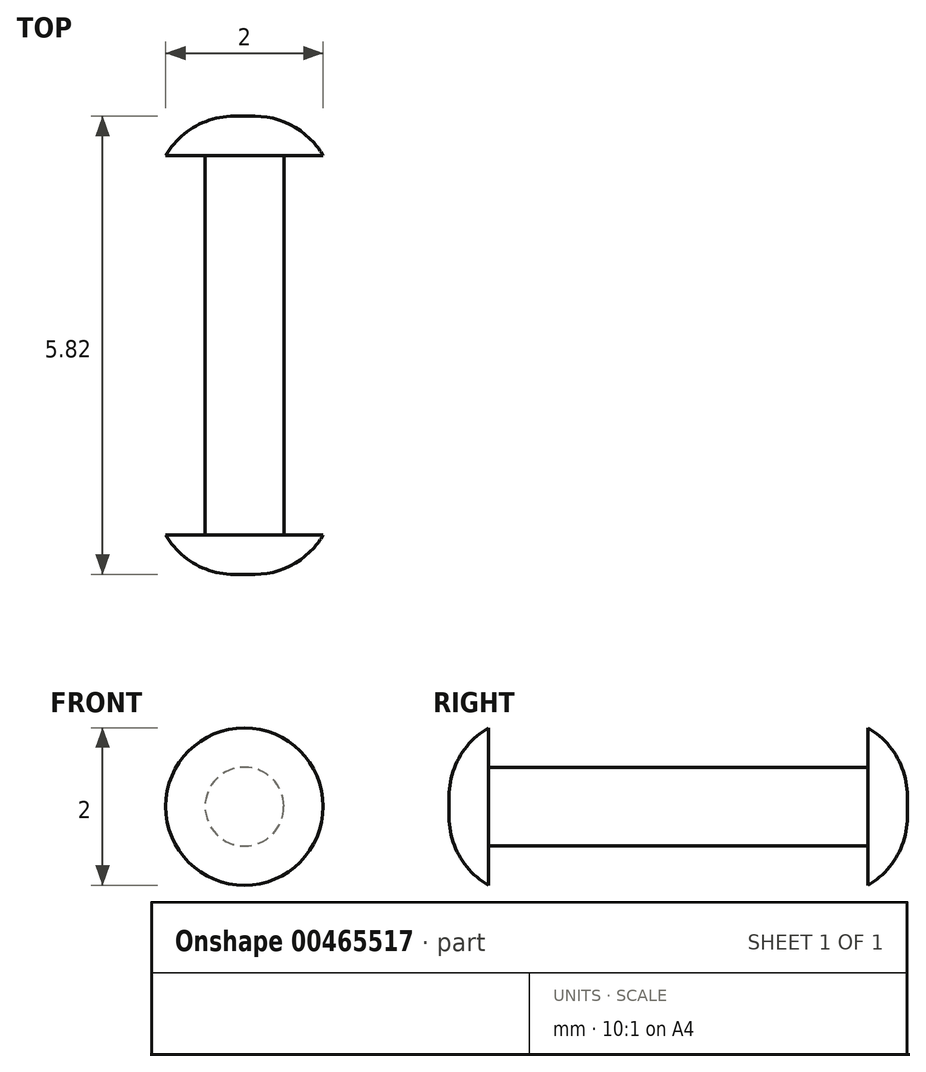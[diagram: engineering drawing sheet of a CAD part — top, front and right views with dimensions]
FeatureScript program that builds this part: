
annotation { "Feature Type Name" : "Feature", "Feature Type Description" : "" }
export const myFeature = defineFeature(function(context is Context, id is Id, definition is map)
    precondition{}
    {
        {
            var Q0;
            Q0=qCreatedBy(makeId("Front.planeOp"),FACE);
            var sketch = newSketch(context, id + "F0", { "sketchPlane" : qUnion([Q0])});
            skCircle(sketch, "E0", {"center": v(0, 0) * mm, "radius": 0.5 * mm});
            skSolve(sketch);
        }
        {
            var Q0;
            Q0 = qSketchRegion(id + "F0", true);
            extrude(context, id + "F1", {"entities" : qUnion([Q0]), "endBound" : BoundingType.SYMMETRIC, "depth" : 4.82 * mm});
        }
        {
            var Q0;
            Q0=makeQuery(id+"F1.opExtrude","CAP_FACE",FACE,{"disambiguationData":[OSD([sQuery(id+"F0.wireOp",EDGE,"E0")])],"isStart":false});
            var sketch = newSketch(context, id + "F2", { "sketchPlane" : qUnion([Q0])});
            skCircle(sketch, "E1", {"center": v(0, 0) * mm, "radius": 1 * mm});
            skSolve(sketch);
        }
        {
            var Q0;
            Q0 = qSketchRegion(id + "F2", true);
            extrude(context, id + "F3", {"entities" : qUnion([Q0]), "operationType" : NewBodyOperationType.ADD, "depth" : 0.5 * mm});
        }
        {
            var Q0;
            Q0=makeQuery(id+"F1.opExtrude","CAP_FACE",FACE,{"disambiguationData":[OSD([sQuery(id+"F0.wireOp",EDGE,"E0")])],"isStart":true});
            var sketch = newSketch(context, id + "F4", { "sketchPlane" : qUnion([Q0])});
            skCircle(sketch, "E2", {"center": v(0, 0) * mm, "radius": 1 * mm});
            skSolve(sketch);
        }
        {
            var Q0;
            Q0 = qSketchRegion(id + "F4", true);
            extrude(context, id + "F5", {"entities" : qUnion([Q0]), "operationType" : NewBodyOperationType.ADD, "depth" : 0.5 * mm});
        }
        {
            var Q0;
            Q0=makeQuery(id+"F5.opExtrude","CAP_EDGE",EDGE,{"disambiguationData":[OSD([sQuery(id+"F4.wireOp",EDGE,"E2")])],"isStart":false});
            var Q1;
            Q1=makeQuery(id+"F3.opExtrude","CAP_EDGE",EDGE,{"disambiguationData":[OSD([sQuery(id+"F2.wireOp",EDGE,"E1")])],"isStart":false});
            fillet(context, id + "F6", {"entities" : qUnion([Q0, Q1]), "radius" : 1 * mm, "allowEdgeOverflow" : false});
        }
    });
